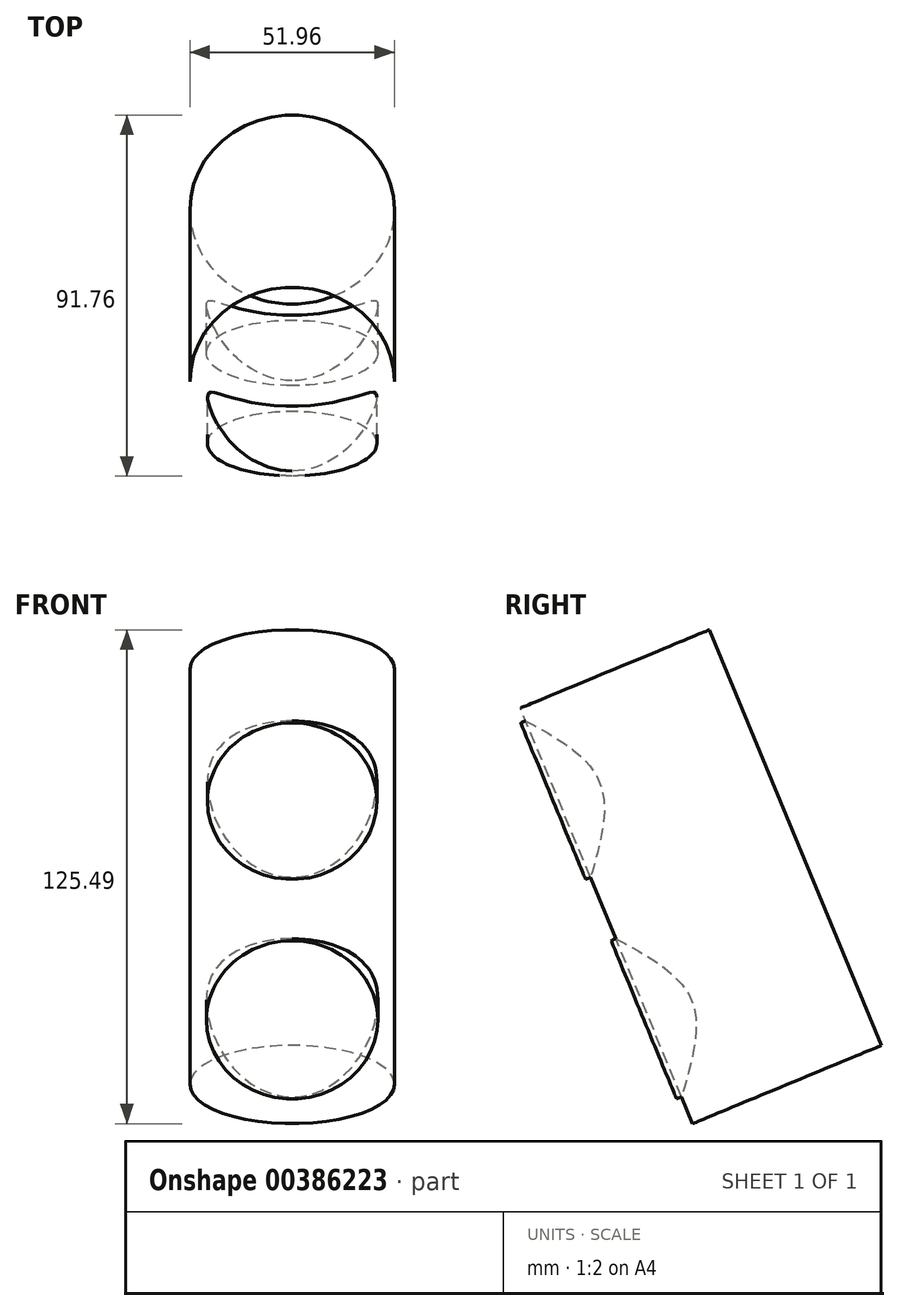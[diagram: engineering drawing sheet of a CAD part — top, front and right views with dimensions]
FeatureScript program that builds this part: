
annotation { "Feature Type Name" : "Feature", "Feature Type Description" : "" }
export const myFeature = defineFeature(function(context is Context, id is Id, definition is map)
    precondition{}
    {
        {
            var Q0;
            Q0=qCreatedBy(makeId("Top.planeOp"),FACE);
            var sketch = newSketch(context, id + "F0", { "sketchPlane" : qUnion([Q0])});
            skCircle(sketch, "E0", {"center": v(0, 27.34) * mm, "radius": 25.98 * mm});
            skSolve(sketch);
        }
        {
            var Q0;
            Q0=sQuery(id+"F0.wireOp",EDGE,"E0");
            extrude(context, id + "F1", {"bodyType" : ToolBodyType.SURFACE, "surfaceEntities" : qUnion([Q0]), "depth" : 114.3 * mm});
        }
        {
            var Q0;
            Q0=qCreatedBy(makeId("Front.planeOp"),FACE);
            var sketch = newSketch(context, id + "F2", { "sketchPlane" : qUnion([Q0])});
            skCircle(sketch, "E1", {"center": v(0, 89.27) * mm, "radius": 21.52 * mm});
            skSolve(sketch);
        }
        {
            var Q0;
            Q0=sQuery(id+"F2.wireOp",EDGE,"E1");
            extrude(context, id + "F3", {"bodyType" : ToolBodyType.SURFACE, "surfaceEntities" : qUnion([Q0]), "endBound" : BoundingType.UP_TO_NEXT, "oppositeDirection" : true, "depth" : 25.4 * mm});
        }
        {
            var Q0;
            Q0=qCreatedBy(makeId("Front.planeOp"),FACE);
            var sketch = newSketch(context, id + "F4", { "sketchPlane" : qUnion([Q0])});
            skCircle(sketch, "E2", {"center": v(0, 29.11) * mm, "radius": 21.76 * mm});
            skSolve(sketch);
        }
        {
            var Q0;
            Q0=sQuery(id+"F4.wireOp",EDGE,"E2");
            extrude(context, id + "F5", {"bodyType" : ToolBodyType.SURFACE, "surfaceEntities" : qUnion([Q0]), "endBound" : BoundingType.UP_TO_NEXT, "oppositeDirection" : true, "depth" : 25.4 * mm});
        }
        {
            var Q0;
            Q0=qCreatedBy(makeId("Right.planeOp"),FACE);
            var sketch = newSketch(context, id + "F6", { "sketchPlane" : qUnion([Q0])});
            skCircle(sketch, "E3", {"center": v(33.53, -35.95) * mm, "radius": 13.97 * mm});
            skSolve(sketch);
        }
        {
            var Q0;
            Q0 = qSketchRegion(id + "F6", true);
            extrude(context, id + "F7", {"entities" : qUnion([Q0]), "depth" : 25.4 * mm});
        }
        {
            var Q0;
            Q0=makeQuery(id+"F3.opExtrude","SWEPT_BODY",BODY,{"disambiguationData":[OSD([sQuery(id+"F2.wireOp",EDGE,"E1")])]});
            var Q1;
            Q1=makeQuery(id+"F5.opExtrude","SWEPT_BODY",BODY,{"disambiguationData":[OSD([sQuery(id+"F4.wireOp",EDGE,"E2")])]});
            var Q2;
            Q2=makeQuery(id+"F1.opExtrude","SWEPT_BODY",BODY,{"disambiguationData":[OSD([sQuery(id+"F0.wireOp",EDGE,"E0")])]});
            var Q3;
            Q3=makeQuery(id+"F7.opExtrude","CAP_EDGE",EDGE,{"disambiguationData":[OSD([sQuery(id+"F6.wireOp",EDGE,"E3")])],"isStart":false});
            transform(context, id + "F8", {"entities" : qUnion([Q0, Q1, Q2]), "transformType" : TransformType.ROTATION, "transformAxis" : qUnion([Q3]), "angle" : 22.5 * degree, "makeCopy" : false});
        }
        {
            var Q0;
            Q0=makeQuery(id+"F7.opExtrude","SWEPT_BODY",BODY,{"disambiguationData":[OSD([sQuery(id+"F6.wireOp",EDGE,"E3")])]});
            deleteBodies(context, id + "F9", {"entities" : qUnion([Q0])});
        }
    });
